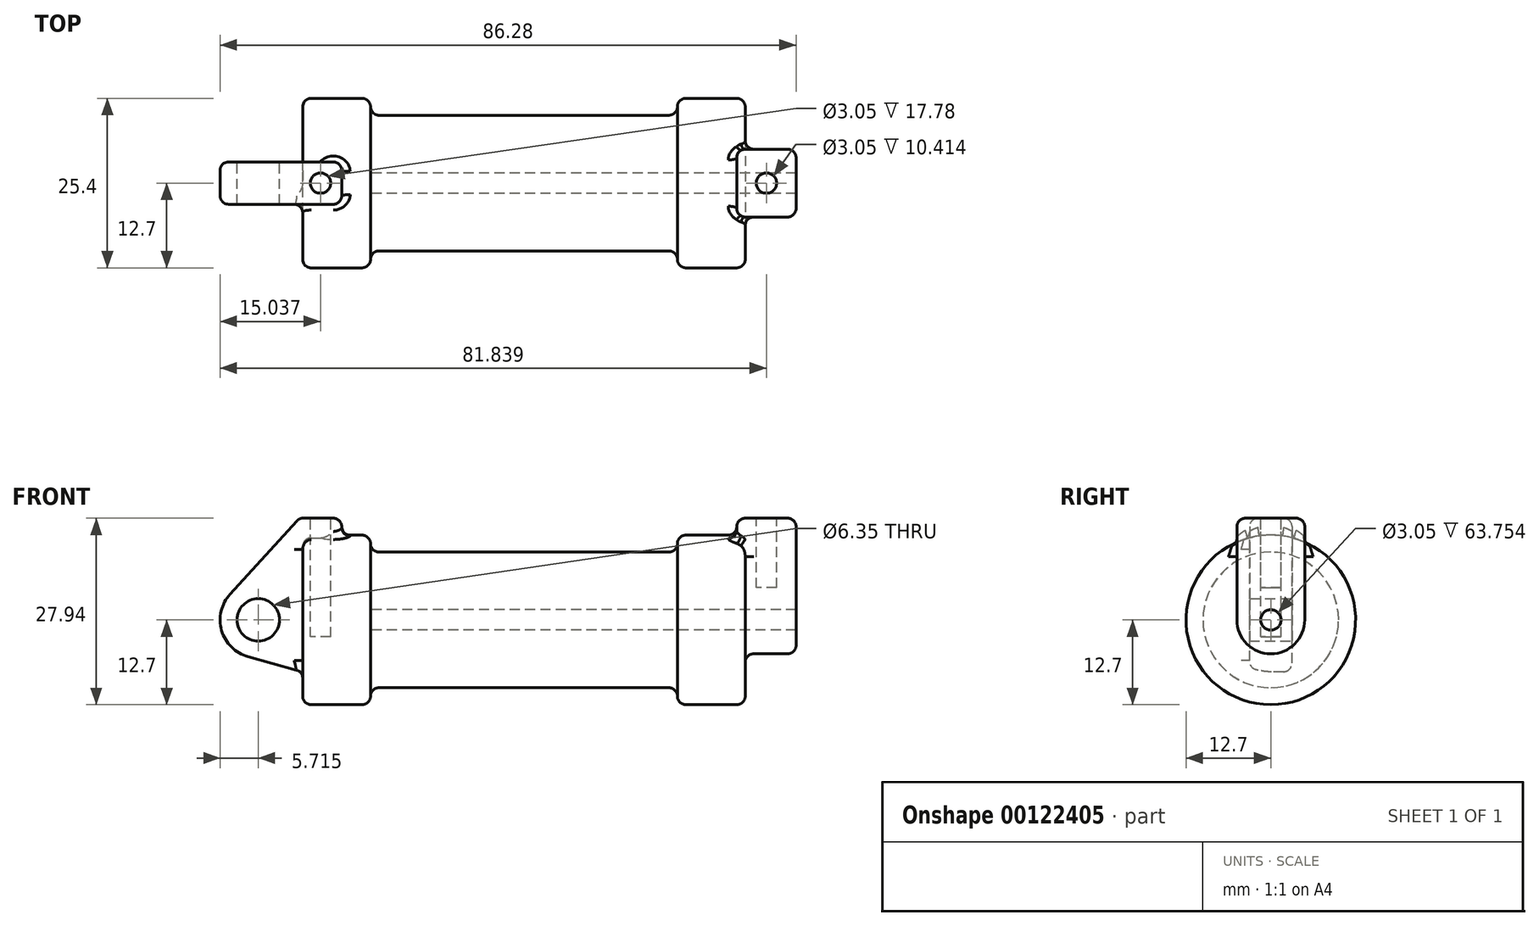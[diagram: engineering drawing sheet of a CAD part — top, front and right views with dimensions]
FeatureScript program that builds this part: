
annotation { "Feature Type Name" : "Feature", "Feature Type Description" : "" }
export const myFeature = defineFeature(function(context is Context, id is Id, definition is map)
    precondition{}
    {
        {
            var Q0;
            Q0=qCreatedBy(makeId("Front.planeOp"),FACE);
            var sketch = newSketch(context, id + "F0", { "sketchPlane" : qUnion([Q0])});
            skLineSegment(sketch, "E0", {"start": v(0, 0) * mm, "end": v(0, 12.7) * mm});
            skLineSegment(sketch, "E1", {"start": v(0, 12.7) * mm, "end": v(10.16, 12.7) * mm});
            skLineSegment(sketch, "E2", {"start": v(10.16, 12.7) * mm, "end": v(10.16, 10.16) * mm});
            skLineSegment(sketch, "E3", {"start": v(10.16, 10.16) * mm, "end": v(56.13, 10.16) * mm});
            skLineSegment(sketch, "E4", {"start": v(56.13, 10.16) * mm, "end": v(56.13, 12.7) * mm});
            skLineSegment(sketch, "E5", {"start": v(56.13, 12.7) * mm, "end": v(66.3, 12.7) * mm});
            skLineSegment(sketch, "E6", {"start": v(66.3, 12.7) * mm, "end": v(66.3, 0) * mm});
            skLineSegment(sketch, "E7", {"start": v(66.3, 0) * mm, "end": v(0, 0) * mm});
            skLineSegment(sketch, "E8", {"start": v(5.84, 15.24) * mm, "end": v(-0.5, 15.24) * mm});
            skLineSegment(sketch, "E9", {"start": v(-0.5, 15.24) * mm, "end": v(-10.88, 3.85) * mm});
            skLineSegment(sketch, "E10", {"start": v(0, 0) * mm, "end": v(-6.65, 0) * mm});
            skCircle(sketch, "E11", {"center": v(-6.65, 0) * mm, "radius": 5.72 * mm});
            skCircle(sketch, "E12", {"center": v(-6.65, 0) * mm, "radius": 3.18 * mm});
            skLineSegment(sketch, "E13", {"start": v(5.84, 15.24) * mm, "end": v(5.84, -9.4) * mm});
            skLineSegment(sketch, "E14", {"start": v(5.84, -9.4) * mm, "end": v(-8.18, -5.5) * mm});
            skSolve(sketch);
        }
        {
            var Q0;
            {var subQ3=sQuery(id+"F0.wireOp",EDGE,"E0");Q0=makeQuery(id+"F0.imprint","IMPRINT",FACE,{"disambiguationData":[TD([[makeQuery(id+"F0.imprint","IMPRINT",EDGE,{"derivedFrom":subQ3}),1.0]])]});}
            var Q1;
            {var subQ4=sQuery(id+"F0.wireOp",EDGE,"E12");Q1=makeQuery(id+"F0.imprint","IMPRINT",FACE,{"disambiguationData":[TD([[makeQuery(id+"F0.imprint","IMPRINT",EDGE,{"derivedFrom":subQ4}),-1.0]])]});}
            var Q2;
            {var subQ0=sQuery(id+"F0.wireOp",EDGE,"E14");Q2=makeQuery(id+"F0.imprint","IMPRINT",FACE,{"disambiguationData":[TD([[makeQuery(id+"F0.imprint","IMPRINT",EDGE,{"derivedFrom":subQ0}),-1.0]])]});}
            var Q3;
            {var subQ0=sQuery(id+"F0.wireOp",EDGE,"E0");Q3=makeQuery(id+"F0.imprint","IMPRINT",FACE,{"disambiguationData":[TD([[makeQuery(id+"F0.imprint","IMPRINT",EDGE,{"derivedFrom":subQ0}),-1.0]])]});}
            extrude(context, id + "F1", {"entities" : qUnion([Q0, Q1, Q2, Q3]), "endBound" : BoundingType.SYMMETRIC, "depth" : 6.35 * mm});
        }
        {
            var Q0;
            {var subQ0=sQuery(id+"F0.wireOp",EDGE,"E2");Q0=makeQuery(id+"F0.imprint","IMPRINT",FACE,{"disambiguationData":[TD([[makeQuery(id+"F0.imprint","IMPRINT",EDGE,{"derivedFrom":subQ0}),-1.0]])]});}
            var Q1;
            {var subQ0=sQuery(id+"F0.wireOp",EDGE,"E0");Q1=makeQuery(id+"F0.imprint","IMPRINT",FACE,{"disambiguationData":[TD([[makeQuery(id+"F0.imprint","IMPRINT",EDGE,{"derivedFrom":subQ0}),-1.0]])]});}
            var Q2;
            Q2=sQuery(id+"F0.wireOp",EDGE,"E7");
            revolve(context, id + "F2", {"entities" : qUnion([Q0, Q1]), "axis" : qUnion([Q2]), "revolveType" : RevolveType.FULL});
        }
        {
            var Q0;
            Q0=makeQuery(id+"F1.opExtrude","SWEPT_BODY",BODY,{"disambiguationData":[OSD([sQuery(id+"F0.wireOp",EDGE,"E8"),sQuery(id+"F0.wireOp",EDGE,"E9"),sQuery(id+"F0.wireOp",EDGE,"E11"),sQuery(id+"F0.wireOp",EDGE,"E12"),sQuery(id+"F0.wireOp",EDGE,"E13"),sQuery(id+"F0.wireOp",EDGE,"E14")])]});
            var Q1;
            Q1=makeQuery(id+"F2.opRevolve","SWEPT_BODY",BODY,{"disambiguationData":[OSD([sQuery(id+"F0.wireOp",EDGE,"E0"),sQuery(id+"F0.wireOp",EDGE,"E1"),sQuery(id+"F0.wireOp",EDGE,"E2"),sQuery(id+"F0.wireOp",EDGE,"E3"),sQuery(id+"F0.wireOp",EDGE,"E4"),sQuery(id+"F0.wireOp",EDGE,"E5"),sQuery(id+"F0.wireOp",EDGE,"E6"),sQuery(id+"F0.wireOp",EDGE,"E7")])]});
            booleanBodies(context, id + "F3", {"operationType" : BooleanOperationType.UNION, "tools" : qUnion([Q0, Q1])});
        }
        {
            var Q0;
            Q0=makeQuery(id+"F2.opRevolve","SWEPT_FACE",FACE,{"disambiguationData":[OSD([sQuery(id+"F0.wireOp",EDGE,"E6")])]});
            var sketch = newSketch(context, id + "F4", { "sketchPlane" : qUnion([Q0])});
            skCircle(sketch, "E15", {"center": v(0, 0) * mm, "radius": 1.52 * mm});
            skCircle(sketch, "E16", {"center": v(0, 0) * mm, "radius": 5.08 * mm});
            skLineSegment(sketch, "E17", {"start": v(-5.08, 0) * mm, "end": v(-5.08, 15.24) * mm});
            skLineSegment(sketch, "E18", {"start": v(-5.08, 15.24) * mm, "end": v(5.08, 15.24) * mm});
            skLineSegment(sketch, "E19", {"start": v(5.08, 15.24) * mm, "end": v(5.08, 0) * mm});
            skSolve(sketch);
        }
        {
            var Q0;
            {var subQ0=sQuery(id+"F4.wireOp",EDGE,"E18");Q0=makeQuery(id+"F4.imprint","IMPRINT",FACE,{"disambiguationData":[TD([[makeQuery(id+"F4.imprint","IMPRINT",EDGE,{"derivedFrom":subQ0}),-1.0]])]});}
            var Q1;
            {var subQ0=sQuery(id+"F4.wireOp",EDGE,"E17");var subQ1=sQuery(id+"F4.wireOp",EDGE,"E16");var subQ2=makeQuery(id+"F4.imprint","INTERSECT",VERTEX,{"derivedFrom":[subQ1,subQ0]});Q1=makeQuery(id+"F4.imprint","IMPRINT",FACE,{"disambiguationData":[TD([[makeQuery(id+"F4.imprint","IMPRINT",EDGE,{"disambiguationData":[TD([[subQ2,1.0]])],"derivedFrom":subQ1}),-1.0]])]});}
            var Q2;
            Q2=makeQuery(id+"F4.imprint","IMPRINT",FACE,{"disambiguationData":[TD([[makeQuery(id+"F4.imprint","IMPRINT",EDGE,{"derivedFrom":sQuery(id+"F4.wireOp",EDGE,"E15")}),-1.0]])]});
            extrude(context, id + "F5", {"entities" : qUnion([Q0, Q1, Q2]), "operationType" : NewBodyOperationType.ADD, "depth" : 7.62 * mm, "hasSecondDirection" : true, "secondDirectionOppositeDirection" : true, "secondDirectionDepth" : 1.27 * mm});
        }
        {
            var Q0;
            Q0=makeQuery(id+"F4.imprint","IMPRINT",FACE,{"disambiguationData":[TD([[makeQuery(id+"F4.imprint","IMPRINT",EDGE,{"derivedFrom":sQuery(id+"F4.wireOp",EDGE,"E15")}),1.0]])]});
            var Q1;
            Q1=makeQuery(id+"F2.opRevolve","SWEPT_FACE",FACE,{"disambiguationData":[OSD([sQuery(id+"F0.wireOp",EDGE,"E2")])]});
            extrude(context, id + "F6", {"entities" : qUnion([Q0]), "operationType" : NewBodyOperationType.REMOVE, "endBound" : BoundingType.UP_TO_SURFACE, "oppositeDirection" : true, "endBoundEntityFace" : qUnion([Q1]), "depth" : 25.4 * mm});
        }
        {
            var Q0;
            Q0=makeQuery(id+"F1.opExtrude","SWEPT_FACE",FACE,{"disambiguationData":[OSD([sQuery(id+"F0.wireOp",EDGE,"E8")])]});
            var sketch = newSketch(context, id + "F7", { "sketchPlane" : qUnion([Q0])});
            skCircle(sketch, "E20", {"center": v(2.67, 0) * mm, "radius": 1.52 * mm});
            skPoint(sketch, "E20.centerSnap0", {"position": v(2.67, 3.18) * mm});
            skPoint(sketch, "E20.centerSnap1", {"position": v(5.84, 0) * mm});
            skLineSegment(sketch, "E21.0.0", {"start": v(65.02, 5.08) * mm, "end": v(65.02, -5.08) * mm, "construction": true});
            skLineSegment(sketch, "E21.0.1", {"start": v(65.02, -5.08) * mm, "end": v(73.91, -5.08) * mm, "construction": true});
            skLineSegment(sketch, "E21.0.2", {"start": v(73.91, -5.08) * mm, "end": v(73.91, 5.08) * mm, "construction": true});
            skLineSegment(sketch, "E21.0.3", {"start": v(73.91, 5.08) * mm, "end": v(65.02, 5.08) * mm, "construction": true});
            skCircle(sketch, "E22", {"center": v(69.47, 0) * mm, "radius": 1.52 * mm});
            skPoint(sketch, "E22.centerSnap0", {"position": v(69.47, 5.08) * mm});
            skPoint(sketch, "E22.centerSnap1", {"position": v(65.02, 0) * mm});
            skSolve(sketch);
        }
        {
            var Q0;
            Q0=makeQuery(id+"F7.imprint","IMPRINT",FACE,{"disambiguationData":[TD([[makeQuery(id+"F7.imprint","IMPRINT",EDGE,{"derivedFrom":sQuery(id+"F7.wireOp",EDGE,"E20")}),1.0]])]});
            extrude(context, id + "F8", {"entities" : qUnion([Q0]), "operationType" : NewBodyOperationType.REMOVE, "oppositeDirection" : true, "depth" : 17.78 * mm});
        }
        {
            var Q0;
            Q0=makeQuery(id+"F7.imprint","IMPRINT",FACE,{"disambiguationData":[TD([[makeQuery(id+"F7.imprint","IMPRINT",EDGE,{"derivedFrom":sQuery(id+"F7.wireOp",EDGE,"E22")}),1.0]])]});
            extrude(context, id + "F9", {"entities" : qUnion([Q0]), "operationType" : NewBodyOperationType.REMOVE, "oppositeDirection" : true, "depth" : 10.4 * mm});
        }
        {
            var Q0;
            Q0=makeQuery(id+"F2.opRevolve","SWEPT_EDGE",EDGE,{"disambiguationData":[OSD([sQuery(id+"F0.wireOp",EDGE,"E2"),sQuery(id+"F0.wireOp",EDGE,"E3")])]});
            var Q1;
            Q1=makeQuery(id+"F2.opRevolve","SWEPT_EDGE",EDGE,{"disambiguationData":[OSD([sQuery(id+"F0.wireOp",EDGE,"E1"),sQuery(id+"F0.wireOp",EDGE,"E2")])]});
            var Q2;
            Q2=makeQuery(id+"F2.opRevolve","SWEPT_EDGE",EDGE,{"disambiguationData":[OSD([sQuery(id+"F0.wireOp",EDGE,"E0"),sQuery(id+"F0.wireOp",EDGE,"E1")])]});
            var Q3;
            Q3=makeQuery(id+"F2.opRevolve","SWEPT_EDGE",EDGE,{"disambiguationData":[OSD([sQuery(id+"F0.wireOp",EDGE,"E3"),sQuery(id+"F0.wireOp",EDGE,"E4")])]});
            var Q4;
            Q4=makeQuery(id+"F2.opRevolve","SWEPT_EDGE",EDGE,{"disambiguationData":[OSD([sQuery(id+"F0.wireOp",EDGE,"E4"),sQuery(id+"F0.wireOp",EDGE,"E5")])]});
            var Q5;
            Q5=makeQuery(id+"F2.opRevolve","SWEPT_EDGE",EDGE,{"disambiguationData":[OSD([sQuery(id+"F0.wireOp",EDGE,"E5"),sQuery(id+"F0.wireOp",EDGE,"E6")])]});
            fillet(context, id + "F10", {"entities" : qUnion([Q0, Q1, Q2, Q3, Q4, Q5]), "radius" : 1.27 * mm, "tangentPropagation" : true, "allowEdgeOverflow" : false});
        }
        {
            var Q0;
            Q0=makeQuery(id+"F1.opExtrude","SWEPT_FACE",FACE,{"disambiguationData":[OSD([sQuery(id+"F0.wireOp",EDGE,"E9")])]});
            var Q1;
            Q1=makeQuery(id+"F1.opExtrude","CAP_EDGE",EDGE,{"disambiguationData":[OSD([sQuery(id+"F0.wireOp",EDGE,"E8")])],"isStart":true});
            var Q2;
            Q2=makeQuery(id+"F1.opExtrude","SWEPT_EDGE",EDGE,{"disambiguationData":[OSD([sQuery(id+"F0.wireOp",EDGE,"E8"),sQuery(id+"F0.wireOp",EDGE,"E13")])]});
            var Q3;
            Q3=makeQuery(id+"F1.opExtrude","CAP_EDGE",EDGE,{"disambiguationData":[OSD([sQuery(id+"F0.wireOp",EDGE,"E8")])],"isStart":false});
            var Q4;
            Q4=makeQuery(id+"F3.opBoolean","INTERSECT",EDGE,{"derivedFrom":[makeQuery(id+"F1.opExtrude","CAP_FACE",FACE,{"disambiguationData":[OSD([sQuery(id+"F0.wireOp",EDGE,"E8"),sQuery(id+"F0.wireOp",EDGE,"E9"),sQuery(id+"F0.wireOp",EDGE,"E11"),sQuery(id+"F0.wireOp",EDGE,"E12"),sQuery(id+"F0.wireOp",EDGE,"E13"),sQuery(id+"F0.wireOp",EDGE,"E14")])],"isStart":false}),makeQuery(id+"F2.opRevolve","SWEPT_FACE",FACE,{"disambiguationData":[OSD([sQuery(id+"F0.wireOp",EDGE,"E0")])]})]});
            var Q5;
            Q5=makeQuery(id+"F3.opBoolean","INTERSECT",EDGE,{"derivedFrom":[makeQuery(id+"F1.opExtrude","SWEPT_FACE",FACE,{"disambiguationData":[OSD([sQuery(id+"F0.wireOp",EDGE,"E13")])]}),makeQuery(id+"F2.opRevolve","SWEPT_FACE",FACE,{"disambiguationData":[OSD([sQuery(id+"F0.wireOp",EDGE,"E1")])]})]});
            var Q6;
            Q6=makeQuery(id+"F1.opExtrude","CAP_EDGE",EDGE,{"disambiguationData":[OSD([sQuery(id+"F0.wireOp",EDGE,"E13")])],"isStart":false});
            var Q7;
            Q7=makeQuery(id+"F1.opExtrude","CAP_EDGE",EDGE,{"disambiguationData":[OSD([sQuery(id+"F0.wireOp",EDGE,"E13")])],"isStart":true});
            fillet(context, id + "F11", {"entities" : qUnion([Q0, Q1, Q2, Q3, Q4, Q5, Q6, Q7]), "radius" : 1.27 * mm, "tangentPropagation" : true, "allowEdgeOverflow" : false});
        }
        {
            var Q0;
            Q0=makeQuery(id+"F5.opExtrude","CAP_EDGE",EDGE,{"disambiguationData":[OSD([sQuery(id+"F4.wireOp",EDGE,"E18")])],"isStart":true});
            var Q1;
            Q1=makeQuery(id+"F5.opExtrude","SWEPT_EDGE",EDGE,{"disambiguationData":[OSD([sQuery(id+"F4.wireOp",EDGE,"E18"),sQuery(id+"F4.wireOp",EDGE,"E19")])]});
            var Q2;
            Q2=makeQuery(id+"F5.opExtrude","CAP_EDGE",EDGE,{"disambiguationData":[OSD([sQuery(id+"F4.wireOp",EDGE,"E18")])],"isStart":false});
            var Q3;
            Q3=makeQuery(id+"F5.opExtrude","SWEPT_EDGE",EDGE,{"disambiguationData":[OSD([sQuery(id+"F4.wireOp",EDGE,"E17"),sQuery(id+"F4.wireOp",EDGE,"E18")])]});
            var Q4;
            Q4=makeQuery(id+"F5.boolean.opBoolean","INTERSECT",EDGE,{"derivedFrom":[makeQuery(id+"F2.opRevolve","SWEPT_FACE",FACE,{"disambiguationData":[OSD([sQuery(id+"F0.wireOp",EDGE,"E5")])]}),makeQuery(id+"F5.opExtrude","CAP_FACE",FACE,{"disambiguationData":[OSD([sQuery(id+"F4.wireOp",EDGE,"E15"),sQuery(id+"F4.wireOp",EDGE,"E16"),sQuery(id+"F4.wireOp",EDGE,"E17"),sQuery(id+"F4.wireOp",EDGE,"E18"),sQuery(id+"F4.wireOp",EDGE,"E19")])],"isStart":true})]});
            var Q5;
            Q5=makeQuery(id+"F5.boolean.opBoolean","INTERSECT",EDGE,{"derivedFrom":[makeQuery(id+"F2.opRevolve","SWEPT_FACE",FACE,{"disambiguationData":[OSD([sQuery(id+"F0.wireOp",EDGE,"E6")])]}),makeQuery(id+"F5.opExtrude","SWEPT_FACE",FACE,{"disambiguationData":[OSD([sQuery(id+"F4.wireOp",EDGE,"E19")])]})]});
            var Q6;
            Q6=makeQuery(id+"F5.opExtrude","CAP_EDGE",EDGE,{"disambiguationData":[OSD([sQuery(id+"F4.wireOp",EDGE,"E19")])],"isStart":false});
            var Q7;
            Q7=makeQuery(id+"F5.opExtrude","CAP_EDGE",EDGE,{"disambiguationData":[OSD([sQuery(id+"F4.wireOp",EDGE,"E17")])],"isStart":true});
            var Q8;
            Q8=makeQuery(id+"F5.opExtrude","CAP_EDGE",EDGE,{"disambiguationData":[OSD([sQuery(id+"F4.wireOp",EDGE,"E19")])],"isStart":true});
            fillet(context, id + "F12", {"entities" : qUnion([Q0, Q1, Q2, Q3, Q4, Q5, Q6, Q7, Q8]), "radius" : 1.27 * mm, "tangentPropagation" : true, "allowEdgeOverflow" : false});
        }
    });
